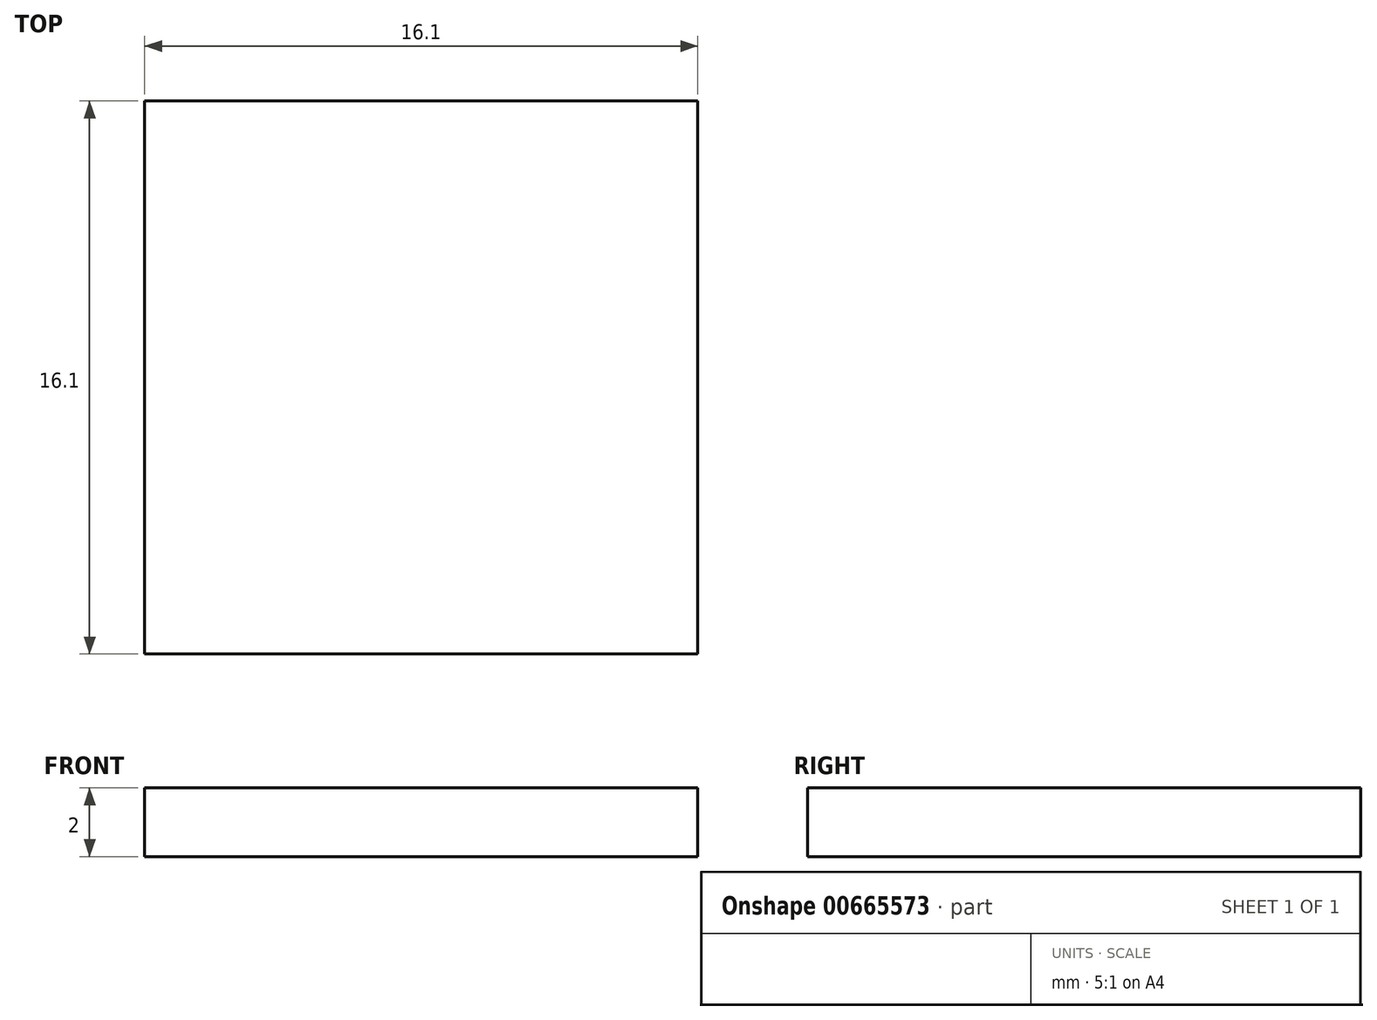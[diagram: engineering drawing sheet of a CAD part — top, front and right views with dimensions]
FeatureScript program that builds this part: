
annotation { "Feature Type Name" : "Feature", "Feature Type Description" : "" }
export const myFeature = defineFeature(function(context is Context, id is Id, definition is map)
    precondition{}
    {
        {
            var Q0;
            Q0=qCreatedBy(makeId("Top.planeOp"),FACE);
            var sketch = newSketch(context, id + "F0", { "sketchPlane" : qUnion([Q0])});
            skLineSegment(sketch, "E0.bottom", {"start": v(8.05, 8.05) * mm, "end": v(-8.05, 8.05) * mm});
            skLineSegment(sketch, "E0.top", {"start": v(8.05, -8.05) * mm, "end": v(-8.05, -8.05) * mm});
            skLineSegment(sketch, "E0.left", {"start": v(8.05, 8.05) * mm, "end": v(8.05, -8.05) * mm});
            skLineSegment(sketch, "E0.right", {"start": v(-8.05, 8.05) * mm, "end": v(-8.05, -8.05) * mm});
            skPoint(sketch, "E0.middle", {"position": v(0, 0) * mm});
            skSolve(sketch);
        }
        {
            var Q0;
            Q0=makeQuery(id+"F0.imprint","IMPRINT",FACE,{"disambiguationData":[TD([[makeQuery(id+"F0.imprint","IMPRINT",EDGE,{"derivedFrom":sQuery(id+"F0.wireOp",EDGE,"E0.bottom")}),1.0]])]});
            extrude(context, id + "F1", {"entities" : qUnion([Q0]), "depth" : 2 * mm, "offsetDistance" : 25.4 * mm});
        }
    });
